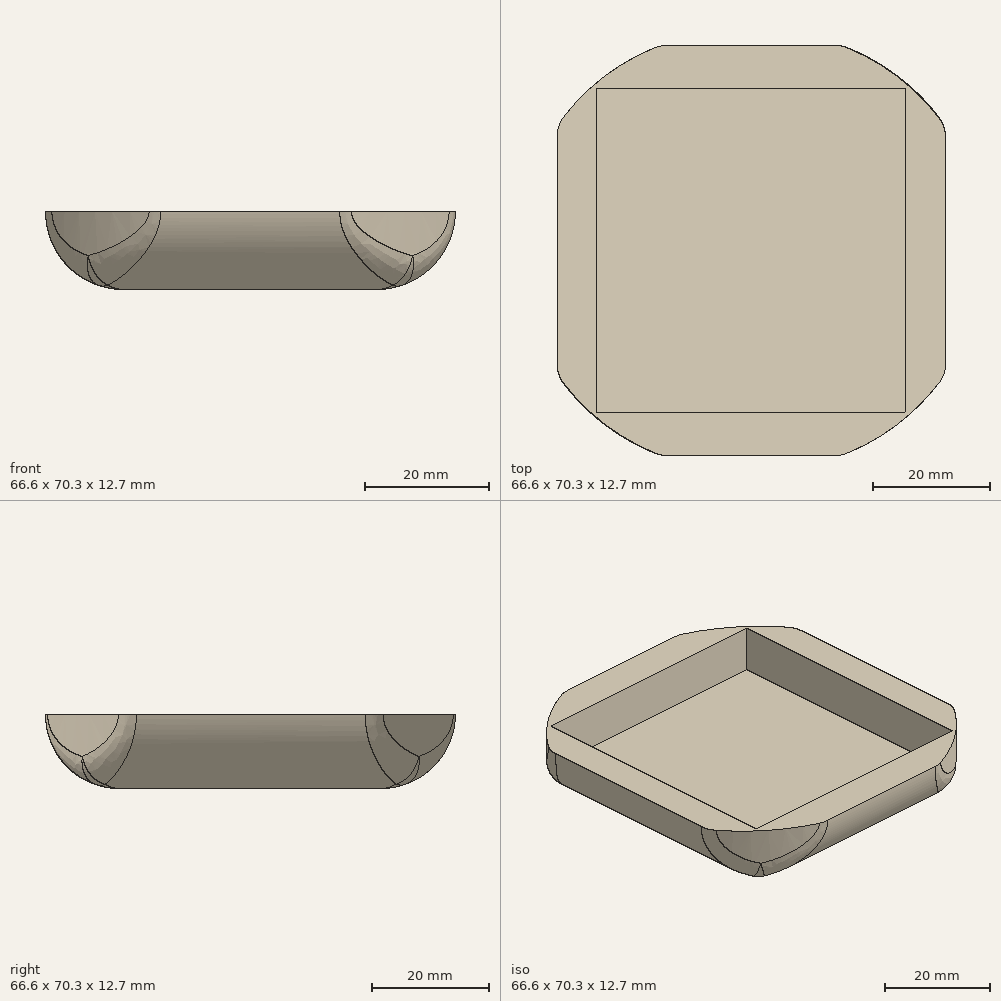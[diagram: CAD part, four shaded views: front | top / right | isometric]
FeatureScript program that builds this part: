
annotation { "Feature Type Name" : "Feature", "Feature Type Description" : "" }
export const myFeature = defineFeature(function(context is Context, id is Id, definition is map)
    precondition{}
    {
        {
            var Q0;
            Q0=qCreatedBy(makeId("Top.planeOp"),FACE);
            var sketch = newSketch(context, id + "F0", { "sketchPlane" : qUnion([Q0])});
            skLineSegment(sketch, "E0.bottom", {"start": v(40, -42.5) * mm, "end": v(-40, -42.5) * mm});
            skLineSegment(sketch, "E0.top", {"start": v(40, 42.5) * mm, "end": v(-40, 42.5) * mm});
            skLineSegment(sketch, "E0.left", {"start": v(40, -42.5) * mm, "end": v(40, 42.5) * mm});
            skLineSegment(sketch, "E0.right", {"start": v(-40, -42.5) * mm, "end": v(-40, 42.5) * mm});
            skPoint(sketch, "E0.middle", {"position": v(0, 0) * mm});
            skSolve(sketch);
        }
        {
            var Q0;
            Q0=makeQuery(id+"F0.imprint","IMPRINT",FACE,{"disambiguationData":[TD([[makeQuery(id+"F0.imprint","IMPRINT",EDGE,{"derivedFrom":sQuery(id+"F0.wireOp",EDGE,"E0.bottom")}),-1.0]])]});
            extrude(context, id + "F1", {"entities" : qUnion([Q0]), "depth" : 25.4 * mm, "offsetDistance" : 25.4 * mm});
        }
        {
            var Q0;
            Q0=qCreatedBy(makeId("Front.planeOp"),FACE);
            var sketch = newSketch(context, id + "F2", { "sketchPlane" : qUnion([Q0])});
            skLineSegment(sketch, "E1.bottom", {"start": v(26.5, 3.57) * mm, "end": v(-26.5, 3.56) * mm});
            skLineSegment(sketch, "E1.top", {"start": v(26.5, 20.57) * mm, "end": v(-26.5, 20.56) * mm});
            skLineSegment(sketch, "E1.left", {"start": v(26.5, 3.57) * mm, "end": v(26.5, 20.57) * mm});
            skLineSegment(sketch, "E1.right", {"start": v(-26.5, 3.56) * mm, "end": v(-26.5, 20.57) * mm});
            skPoint(sketch, "E1.middle", {"position": v(0, 12.07) * mm});
            skSolve(sketch);
        }
        {
            var Q0;
            Q0=qSketchRegion(id+"F2",true);
            extrude(context, id + "F3", {"entities" : qUnion([Q0]), "operationType" : NewBodyOperationType.REMOVE, "oppositeDirection" : true, "depth" : 55.55 * mm, "offsetDistance" : 25.4 * mm, "symmetric" : true});
        }
        {
            var Q0;
            Q0=makeQuery(id+"F1.opExtrude","CAP_FACE",FACE,{"disambiguationData":[OSD([sQuery(id+"F0.wireOp",EDGE,"E0.bottom"),sQuery(id+"F0.wireOp",EDGE,"E0.top"),sQuery(id+"F0.wireOp",EDGE,"E0.left"),sQuery(id+"F0.wireOp",EDGE,"E0.right")])],"isStart":false});
            var sketch = newSketch(context, id + "F4", { "sketchPlane" : qUnion([Q0])});
            skLineSegment(sketch, "E2.bottom", {"start": v(40, -42.5) * mm, "end": v(-40, -42.5) * mm});
            skLineSegment(sketch, "E2.top", {"start": v(40, 42.5) * mm, "end": v(-40, 42.5) * mm});
            skLineSegment(sketch, "E2.left", {"start": v(40, -42.5) * mm, "end": v(40, 42.5) * mm});
            skLineSegment(sketch, "E2.right", {"start": v(-40, -42.5) * mm, "end": v(-40, 42.5) * mm});
            skPoint(sketch, "E2.middle", {"position": v(0, 0) * mm});
            skSolve(sketch);
        }
        {
            var Q0;
            Q0=qSketchRegion(id+"F4",true);
            extrude(context, id + "F5", {"entities" : qUnion([Q0]), "operationType" : NewBodyOperationType.REMOVE, "oppositeDirection" : true, "depth" : 12.7 * mm, "offsetDistance" : 25.4 * mm});
        }
        {
            var Q0;
            Q0=makeQuery(id+"F1.opExtrude","SWEPT_EDGE",EDGE,{"disambiguationData":[OSD([sQuery(id+"F0.wireOp",EDGE,"E0.bottom"),sQuery(id+"F0.wireOp",EDGE,"E0.right")])]});
            fillet(context, id + "F6", {"entities" : qUnion([Q0]), "radius" : 7.62 * mm, "tangentPropagation" : true, "allowEdgeOverflow" : false});
        }
        {
            var Q0;
            Q0=makeQuery(id+"F1.opExtrude","SWEPT_EDGE",EDGE,{"disambiguationData":[OSD([sQuery(id+"F0.wireOp",EDGE,"E0.top"),sQuery(id+"F0.wireOp",EDGE,"E0.right")])]});
            fillet(context, id + "F7", {"entities" : qUnion([Q0]), "radius" : 7.62 * mm, "tangentPropagation" : true, "allowEdgeOverflow" : false});
        }
        {
            var Q0;
            Q0=makeQuery(id+"F1.opExtrude","SWEPT_EDGE",EDGE,{"disambiguationData":[OSD([sQuery(id+"F0.wireOp",EDGE,"E0.top"),sQuery(id+"F0.wireOp",EDGE,"E0.left")])]});
            fillet(context, id + "F8", {"entities" : qUnion([Q0]), "radius" : 7.62 * mm, "tangentPropagation" : true, "allowEdgeOverflow" : false});
        }
        {
            var Q0;
            Q0=makeQuery(id+"F1.opExtrude","SWEPT_EDGE",EDGE,{"disambiguationData":[OSD([sQuery(id+"F0.wireOp",EDGE,"E0.bottom"),sQuery(id+"F0.wireOp",EDGE,"E0.left")])]});
            fillet(context, id + "F9", {"entities" : qUnion([Q0]), "radius" : 7.62 * mm, "tangentPropagation" : true, "allowEdgeOverflow" : false});
        }
        {
            var Q0;
            Q0=makeQuery(id+"F3.boolean.opBoolean","COPY",FACE,{"derivedFrom":makeQuery(id+"F3.opExtrude","SWEPT_FACE",FACE,{"disambiguationData":[OSD([sQuery(id+"F2.wireOp",EDGE,"E1.bottom")])]})});
            var sketch = newSketch(context, id + "F10", { "sketchPlane" : qUnion([Q0])});
            skLineSegment(sketch, "E3", {"start": v(26.5, -42.5) * mm, "end": v(22.69, -35.14) * mm});
            skLineSegment(sketch, "E4", {"start": v(-22.69, -35.14) * mm, "end": v(-26.5, -42.5) * mm});
            skLineSegment(sketch, "E5", {"start": v(40, -27.77) * mm, "end": v(33.33, -24) * mm});
            skLineSegment(sketch, "E6", {"start": v(33.25, 23.96) * mm, "end": v(33.33, -24) * mm});
            skLineSegment(sketch, "E7", {"start": v(40, 27.77) * mm, "end": v(33.25, 23.96) * mm});
            skLineSegment(sketch, "E8", {"start": v(-22.69, 35.14) * mm, "end": v(22.69, 35.14) * mm});
            skLineSegment(sketch, "E9", {"start": v(26.5, 42.5) * mm, "end": v(22.69, 35.14) * mm});
            skLineSegment(sketch, "E10", {"start": v(-26.5, 42.5) * mm, "end": v(-22.69, 35.14) * mm});
            skLineSegment(sketch, "E11", {"start": v(-33.25, 23.96) * mm, "end": v(-33.25, -23.96) * mm});
            skLineSegment(sketch, "E12", {"start": v(-40, 27.77) * mm, "end": v(-33.25, 23.96) * mm});
            skLineSegment(sketch, "E13", {"start": v(-40, -27.77) * mm, "end": v(-33.25, -23.96) * mm});
            skLineSegment(sketch, "E14", {"start": v(40, -27.77) * mm, "end": v(40, 27.77) * mm});
            skLineSegment(sketch, "E15", {"start": v(26.5, 42.5) * mm, "end": v(-26.5, 42.5) * mm});
            skLineSegment(sketch, "E16", {"start": v(-40, 27.77) * mm, "end": v(-40, -27.77) * mm});
            skLineSegment(sketch, "E17", {"start": v(-26.5, -42.5) * mm, "end": v(26.5, -42.5) * mm});
            skLineSegment(sketch, "E18", {"start": v(22.69, -35.14) * mm, "end": v(-22.69, -35.14) * mm});
            skLineSegment(sketch, "E19", {"start": v(40, 27.77) * mm, "end": v(40, -27.77) * mm});
            skSolve(sketch);
        }
        {
            var Q0;
            Q0=qSketchRegion(id+"F10",true);
            extrude(context, id + "F11", {"entities" : qUnion([Q0]), "operationType" : NewBodyOperationType.REMOVE, "depth" : 25.4 * mm, "offsetDistance" : 25.4 * mm, "symmetric" : true});
        }
        {
            var Q0;
            Q0=makeQuery(id+"F1.opExtrude","CAP_FACE",FACE,{"disambiguationData":[OSD([sQuery(id+"F0.wireOp",EDGE,"E0.bottom"),sQuery(id+"F0.wireOp",EDGE,"E0.top"),sQuery(id+"F0.wireOp",EDGE,"E0.left"),sQuery(id+"F0.wireOp",EDGE,"E0.right")])],"isStart":true});
            var sketch = newSketch(context, id + "F12", { "sketchPlane" : qUnion([Q0])});
            skPoint(sketch, "E20.middle", {"position": v(0, 0) * mm});
            skPoint(sketch, "E21.endSnap0", {"position": v(0, 30.06) * mm});
            skLineSegment(sketch, "E22", {"start": v(-15.46, 35.14) * mm, "end": v(0, 35.14) * mm});
            skLineSegment(sketch, "E23", {"start": v(-15.46, 35.14) * mm, "end": v(15.46, 35.14) * mm});
            skLineSegment(sketch, "E24", {"start": v(-15.46, -35.14) * mm, "end": v(15.46, -35.14) * mm});
            skCircle(sketch, "E25", {"center": v(0, 0) * mm, "radius": 62.24 * mm});
            skArc(sketch, "E26", {"start": v(-15.46, 35.14) * mm, "mid": v(-39.89, 0) * mm, "end": v(-15.46, -35.14) * mm});
            skArc(sketch, "E27", {"start": v(15.46, 35.14) * mm, "mid": v(39.89, 0) * mm, "end": v(15.46, -35.14) * mm});
            skSolve(sketch);
        }
        {
            var Q0;
            {var subQ1=sQuery(id+"F0.wireOp",EDGE,"E0.right");var subQ2=sQuery(id+"F0.wireOp",EDGE,"E0.left");var subQ3=sQuery(id+"F0.wireOp",EDGE,"E0.top");var subQ4=sQuery(id+"F0.wireOp",EDGE,"E0.bottom");var subQ5=makeQuery(id+"F1.opExtrude","CAP_FACE",FACE,{"disambiguationData":[OSD([subQ4,subQ3,subQ2,subQ1])],"isStart":true});var subQ6=subQ5;var subQ7=subQ6;var subQ8=subQ7;var subQ9=subQ8;var subQ13=makeQuery(id+"F11.opExtrude","SWEPT_FACE",FACE,{"disambiguationData":[OSD([sQuery(id+"F10.wireOp",EDGE,"E4")])]});var subQ14=makeQuery(id+"F11.boolean.opBoolean","INTERSECT",EDGE,{"derivedFrom":[subQ9,subQ13]});var subQ15=makeQuery(id+"F12.imprint","IMPRINT",EDGE,{"derivedFrom":subQ14});var subQ21=sQuery(id+"F12.wireOp",EDGE,"E22");var subQ35=makeQuery(id+"F11.opExtrude","SWEPT_FACE",FACE,{"disambiguationData":[OSD([sQuery(id+"F10.wireOp",EDGE,"E10")])]});var subQ36=makeQuery(id+"F11.boolean.opBoolean","INTERSECT",EDGE,{"derivedFrom":[subQ9,subQ35]});var subQ41=makeQuery(id+"F12.imprint","IMPRINT",EDGE,{"derivedFrom":subQ36});var subQ52=makeQuery(id+"F11.opExtrude","SWEPT_FACE",FACE,{"disambiguationData":[OSD([sQuery(id+"F10.wireOp",EDGE,"E7")])]});var subQ53=makeQuery(id+"F11.boolean.opBoolean","INTERSECT",EDGE,{"derivedFrom":[subQ9,subQ52]});var subQ54=makeQuery(id+"F12.imprint","IMPRINT",EDGE,{"derivedFrom":subQ53});var subQ70=makeQuery(id+"F11.opExtrude","SWEPT_FACE",FACE,{"disambiguationData":[OSD([sQuery(id+"F10.wireOp",EDGE,"E3")])]});var subQ71=makeQuery(id+"F11.boolean.opBoolean","INTERSECT",EDGE,{"derivedFrom":[subQ9,subQ70]});var subQ72=makeQuery(id+"F12.imprint","IMPRINT",EDGE,{"derivedFrom":subQ71});Q0=qUnion([makeQuery(id+"F12.imprint","IMPRINT",FACE,{"disambiguationData":[TD([[subQ72,-1.0]])]}),makeQuery(id+"F12.imprint","IMPRINT",FACE,{"disambiguationData":[TD([[makeQuery(id+"F12.imprint","IMPRINT",EDGE,{"derivedFrom":subQ21}),1.0]])]}),makeQuery(id+"F12.imprint","IMPRINT",FACE,{"disambiguationData":[TD([[subQ54,-1.0]])]}),makeQuery(id+"F12.imprint","IMPRINT",FACE,{"disambiguationData":[TD([[subQ41,-1.0]])]}),makeQuery(id+"F12.imprint","IMPRINT",FACE,{"disambiguationData":[TD([[subQ15,-1.0]])]})]);}
            extrude(context, id + "F13", {"entities" : qUnion([Q0]), "operationType" : NewBodyOperationType.REMOVE, "oppositeDirection" : true, "depth" : 25.4 * mm, "offsetDistance" : 25.4 * mm});
        }
        {
            var Q0;
            Q0=makeQuery(id+"F11.boolean.opBoolean","INTERSECT",EDGE,{"derivedFrom":[makeQuery(id+"F1.opExtrude","CAP_FACE",FACE,{"disambiguationData":[OSD([sQuery(id+"F0.wireOp",EDGE,"E0.bottom"),sQuery(id+"F0.wireOp",EDGE,"E0.top"),sQuery(id+"F0.wireOp",EDGE,"E0.left"),sQuery(id+"F0.wireOp",EDGE,"E0.right")])],"isStart":true}),makeQuery(id+"F11.opExtrude","SWEPT_FACE",FACE,{"disambiguationData":[OSD([sQuery(id+"F10.wireOp",EDGE,"E18")])]})]});
            fillet(context, id + "F14", {"entities" : qUnion([Q0]), "radius" : 12.7 * mm, "tangentPropagation" : true, "allowEdgeOverflow" : false});
        }
        {
            var Q0;
            Q0=makeQuery(id+"F11.boolean.opBoolean","INTERSECT",EDGE,{"derivedFrom":[makeQuery(id+"F1.opExtrude","CAP_FACE",FACE,{"disambiguationData":[OSD([sQuery(id+"F0.wireOp",EDGE,"E0.bottom"),sQuery(id+"F0.wireOp",EDGE,"E0.top"),sQuery(id+"F0.wireOp",EDGE,"E0.left"),sQuery(id+"F0.wireOp",EDGE,"E0.right")])],"isStart":true}),makeQuery(id+"F11.opExtrude","SWEPT_FACE",FACE,{"disambiguationData":[OSD([sQuery(id+"F10.wireOp",EDGE,"E6")])]})]});
            fillet(context, id + "F15", {"entities" : qUnion([Q0]), "radius" : 12.7 * mm, "tangentPropagation" : true, "allowEdgeOverflow" : false});
        }
        {
            var Q0;
            Q0=makeQuery(id+"F11.boolean.opBoolean","INTERSECT",EDGE,{"derivedFrom":[makeQuery(id+"F1.opExtrude","CAP_FACE",FACE,{"disambiguationData":[OSD([sQuery(id+"F0.wireOp",EDGE,"E0.bottom"),sQuery(id+"F0.wireOp",EDGE,"E0.top"),sQuery(id+"F0.wireOp",EDGE,"E0.left"),sQuery(id+"F0.wireOp",EDGE,"E0.right")])],"isStart":true}),makeQuery(id+"F11.opExtrude","SWEPT_FACE",FACE,{"disambiguationData":[OSD([sQuery(id+"F10.wireOp",EDGE,"E8")])]})]});
            fillet(context, id + "F16", {"entities" : qUnion([Q0]), "radius" : 12.7 * mm, "tangentPropagation" : true, "allowEdgeOverflow" : false});
        }
        {
            var Q0;
            Q0=makeQuery(id+"F11.boolean.opBoolean","INTERSECT",EDGE,{"derivedFrom":[makeQuery(id+"F1.opExtrude","CAP_FACE",FACE,{"disambiguationData":[OSD([sQuery(id+"F0.wireOp",EDGE,"E0.bottom"),sQuery(id+"F0.wireOp",EDGE,"E0.top"),sQuery(id+"F0.wireOp",EDGE,"E0.left"),sQuery(id+"F0.wireOp",EDGE,"E0.right")])],"isStart":true}),makeQuery(id+"F11.opExtrude","SWEPT_FACE",FACE,{"disambiguationData":[OSD([sQuery(id+"F10.wireOp",EDGE,"E11")])]})]});
            fillet(context, id + "F17", {"entities" : qUnion([Q0]), "radius" : 12.7 * mm, "tangentPropagation" : true, "allowEdgeOverflow" : false});
        }
        {
            var Q0;
            {var subQ0=makeQuery(id+"F1.opExtrude","CAP_FACE",FACE,{"disambiguationData":[OSD([sQuery(id+"F0.wireOp",EDGE,"E0.bottom"),sQuery(id+"F0.wireOp",EDGE,"E0.top"),sQuery(id+"F0.wireOp",EDGE,"E0.left"),sQuery(id+"F0.wireOp",EDGE,"E0.right")])],"isStart":true});var subQ1=makeQuery(id+"F11.opExtrude","SWEPT_FACE",FACE,{"disambiguationData":[OSD([sQuery(id+"F10.wireOp",EDGE,"E6")])]});Q0=makeQuery(id+"F15.opFillet","BLEND_EDGE",EDGE,{"blendedFrom":[makeQuery(id+"F11.boolean.opBoolean","INTERSECT",EDGE,{"derivedFrom":[subQ0,subQ1]}),makeQuery(id+"F13.boolean.opBoolean","COPY",FACE,{"disambiguationData":[TD([makeQuery(id+"F11.boolean.opBoolean","COPY",FACE,{"derivedFrom":makeQuery(id+"F11.opExtrude","SWEPT_FACE",FACE,{"disambiguationData":[OSD([sQuery(id+"F10.wireOp",EDGE,"E18")])]})})])],"derivedFrom":makeQuery(id+"F13.opExtrude","SWEPT_FACE",FACE,{"disambiguationData":[OSD([sQuery(id+"F12.wireOp",EDGE,"E27")])]})})],"blendedInto":[makeQuery(id+"F13.boolean.opBoolean","COPY",FACE,{"disambiguationData":[TD([makeQuery(id+"F11.boolean.opBoolean","COPY",FACE,{"derivedFrom":makeQuery(id+"F11.opExtrude","SWEPT_FACE",FACE,{"disambiguationData":[OSD([sQuery(id+"F10.wireOp",EDGE,"E18")])]})})])],"derivedFrom":makeQuery(id+"F13.opExtrude","SWEPT_FACE",FACE,{"disambiguationData":[OSD([sQuery(id+"F12.wireOp",EDGE,"E27")])]})})]});}
            fillet(context, id + "F18", {"entities" : qUnion([Q0]), "radius" : 5.08 * mm, "tangentPropagation" : true, "allowEdgeOverflow" : false});
        }
        {
            var Q0;
            {var subQ0=sQuery(id+"F10.wireOp",EDGE,"E18");var subQ1=sQuery(id+"F0.wireOp",EDGE,"E0.right");var subQ2=sQuery(id+"F0.wireOp",EDGE,"E0.left");var subQ3=sQuery(id+"F0.wireOp",EDGE,"E0.top");var subQ4=sQuery(id+"F0.wireOp",EDGE,"E0.bottom");var subQ5=makeQuery(id+"F1.opExtrude","CAP_FACE",FACE,{"disambiguationData":[OSD([subQ4,subQ3,subQ2,subQ1])],"isStart":true});var subQ6=makeQuery(id+"F11.opExtrude","SWEPT_FACE",FACE,{"disambiguationData":[OSD([sQuery(id+"F10.wireOp",EDGE,"E6")])]});Q0=makeQuery(id+"F18.opFillet","BLEND_EDGE",EDGE,{"blendedFrom":[makeQuery(id+"F15.opFillet","BLEND_EDGE",EDGE,{"blendedFrom":[makeQuery(id+"F11.boolean.opBoolean","INTERSECT",EDGE,{"derivedFrom":[subQ5,subQ6]}),makeQuery(id+"F13.boolean.opBoolean","COPY",FACE,{"disambiguationData":[TD([makeQuery(id+"F11.boolean.opBoolean","COPY",FACE,{"derivedFrom":makeQuery(id+"F11.opExtrude","SWEPT_FACE",FACE,{"disambiguationData":[OSD([subQ0])]})})])],"derivedFrom":makeQuery(id+"F13.opExtrude","SWEPT_FACE",FACE,{"disambiguationData":[OSD([sQuery(id+"F12.wireOp",EDGE,"E27")])]})})],"blendedInto":[makeQuery(id+"F13.boolean.opBoolean","COPY",FACE,{"disambiguationData":[TD([makeQuery(id+"F11.boolean.opBoolean","COPY",FACE,{"derivedFrom":makeQuery(id+"F11.opExtrude","SWEPT_FACE",FACE,{"disambiguationData":[OSD([subQ0])]})})])],"derivedFrom":makeQuery(id+"F13.opExtrude","SWEPT_FACE",FACE,{"disambiguationData":[OSD([sQuery(id+"F12.wireOp",EDGE,"E27")])]})})]}),makeQuery(id+"F14.opFillet","BLEND_FACE",FACE,{"disambiguationData":[OSD([subQ4,subQ3,subQ2,subQ1,subQ0])]})],"blendedInto":[makeQuery(id+"F14.opFillet","BLEND_FACE",FACE,{"disambiguationData":[OSD([subQ4,subQ3,subQ2,subQ1,subQ0])]})]});}
            fillet(context, id + "F19", {"entities" : qUnion([Q0]), "radius" : 5.08 * mm, "tangentPropagation" : true, "allowEdgeOverflow" : false});
        }
        {
            var Q0;
            {var subQ0=makeQuery(id+"F1.opExtrude","CAP_FACE",FACE,{"disambiguationData":[OSD([sQuery(id+"F0.wireOp",EDGE,"E0.bottom"),sQuery(id+"F0.wireOp",EDGE,"E0.top"),sQuery(id+"F0.wireOp",EDGE,"E0.left"),sQuery(id+"F0.wireOp",EDGE,"E0.right")])],"isStart":true});var subQ1=makeQuery(id+"F11.opExtrude","SWEPT_FACE",FACE,{"disambiguationData":[OSD([sQuery(id+"F10.wireOp",EDGE,"E6")])]});Q0=makeQuery(id+"F15.opFillet","BLEND_EDGE",EDGE,{"blendedFrom":[makeQuery(id+"F11.boolean.opBoolean","INTERSECT",EDGE,{"derivedFrom":[subQ0,subQ1]}),makeQuery(id+"F13.boolean.opBoolean","COPY",FACE,{"disambiguationData":[TD([makeQuery(id+"F11.boolean.opBoolean","COPY",FACE,{"derivedFrom":makeQuery(id+"F11.opExtrude","SWEPT_FACE",FACE,{"disambiguationData":[OSD([sQuery(id+"F10.wireOp",EDGE,"E8")])]})})])],"derivedFrom":makeQuery(id+"F13.opExtrude","SWEPT_FACE",FACE,{"disambiguationData":[OSD([sQuery(id+"F12.wireOp",EDGE,"E27")])]})})],"blendedInto":[makeQuery(id+"F13.boolean.opBoolean","COPY",FACE,{"disambiguationData":[TD([makeQuery(id+"F11.boolean.opBoolean","COPY",FACE,{"derivedFrom":makeQuery(id+"F11.opExtrude","SWEPT_FACE",FACE,{"disambiguationData":[OSD([sQuery(id+"F10.wireOp",EDGE,"E8")])]})})])],"derivedFrom":makeQuery(id+"F13.opExtrude","SWEPT_FACE",FACE,{"disambiguationData":[OSD([sQuery(id+"F12.wireOp",EDGE,"E27")])]})})]});}
            fillet(context, id + "F20", {"entities" : qUnion([Q0]), "radius" : 5.08 * mm, "tangentPropagation" : true, "allowEdgeOverflow" : false});
        }
        {
            var Q0;
            {var subQ0=makeQuery(id+"F1.opExtrude","CAP_FACE",FACE,{"disambiguationData":[OSD([sQuery(id+"F0.wireOp",EDGE,"E0.bottom"),sQuery(id+"F0.wireOp",EDGE,"E0.top"),sQuery(id+"F0.wireOp",EDGE,"E0.left"),sQuery(id+"F0.wireOp",EDGE,"E0.right")])],"isStart":true});var subQ1=makeQuery(id+"F11.opExtrude","SWEPT_FACE",FACE,{"disambiguationData":[OSD([sQuery(id+"F10.wireOp",EDGE,"E8")])]});Q0=makeQuery(id+"F16.opFillet","BLEND_EDGE",EDGE,{"blendedFrom":[makeQuery(id+"F11.boolean.opBoolean","INTERSECT",EDGE,{"derivedFrom":[subQ0,subQ1]}),makeQuery(id+"F13.boolean.opBoolean","COPY",FACE,{"disambiguationData":[TD([makeQuery(id+"F11.boolean.opBoolean","COPY",FACE,{"derivedFrom":subQ1})])],"derivedFrom":makeQuery(id+"F13.opExtrude","SWEPT_FACE",FACE,{"disambiguationData":[OSD([sQuery(id+"F12.wireOp",EDGE,"E27")])]})})],"blendedInto":[makeQuery(id+"F13.boolean.opBoolean","COPY",FACE,{"disambiguationData":[TD([makeQuery(id+"F11.boolean.opBoolean","COPY",FACE,{"derivedFrom":subQ1})])],"derivedFrom":makeQuery(id+"F13.opExtrude","SWEPT_FACE",FACE,{"disambiguationData":[OSD([sQuery(id+"F12.wireOp",EDGE,"E27")])]})})]});}
            fillet(context, id + "F21", {"entities" : qUnion([Q0]), "radius" : 5.08 * mm, "tangentPropagation" : true, "allowEdgeOverflow" : false});
        }
        {
            var Q0;
            {var subQ0=makeQuery(id+"F1.opExtrude","CAP_FACE",FACE,{"disambiguationData":[OSD([sQuery(id+"F0.wireOp",EDGE,"E0.bottom"),sQuery(id+"F0.wireOp",EDGE,"E0.top"),sQuery(id+"F0.wireOp",EDGE,"E0.left"),sQuery(id+"F0.wireOp",EDGE,"E0.right")])],"isStart":true});var subQ1=makeQuery(id+"F11.opExtrude","SWEPT_FACE",FACE,{"disambiguationData":[OSD([sQuery(id+"F10.wireOp",EDGE,"E8")])]});Q0=makeQuery(id+"F16.opFillet","BLEND_EDGE",EDGE,{"blendedFrom":[makeQuery(id+"F11.boolean.opBoolean","INTERSECT",EDGE,{"derivedFrom":[subQ0,subQ1]}),makeQuery(id+"F13.boolean.opBoolean","COPY",FACE,{"disambiguationData":[TD([makeQuery(id+"F11.boolean.opBoolean","COPY",FACE,{"derivedFrom":subQ1})])],"derivedFrom":makeQuery(id+"F13.opExtrude","SWEPT_FACE",FACE,{"disambiguationData":[OSD([sQuery(id+"F12.wireOp",EDGE,"E26")])]})})],"blendedInto":[makeQuery(id+"F13.boolean.opBoolean","COPY",FACE,{"disambiguationData":[TD([makeQuery(id+"F11.boolean.opBoolean","COPY",FACE,{"derivedFrom":subQ1})])],"derivedFrom":makeQuery(id+"F13.opExtrude","SWEPT_FACE",FACE,{"disambiguationData":[OSD([sQuery(id+"F12.wireOp",EDGE,"E26")])]})})]});}
            fillet(context, id + "F22", {"entities" : qUnion([Q0]), "radius" : 5.08 * mm, "tangentPropagation" : true, "allowEdgeOverflow" : false});
        }
        {
            var Q0;
            {var subQ0=makeQuery(id+"F1.opExtrude","CAP_FACE",FACE,{"disambiguationData":[OSD([sQuery(id+"F0.wireOp",EDGE,"E0.bottom"),sQuery(id+"F0.wireOp",EDGE,"E0.top"),sQuery(id+"F0.wireOp",EDGE,"E0.left"),sQuery(id+"F0.wireOp",EDGE,"E0.right")])],"isStart":true});var subQ1=makeQuery(id+"F11.opExtrude","SWEPT_FACE",FACE,{"disambiguationData":[OSD([sQuery(id+"F10.wireOp",EDGE,"E11")])]});Q0=makeQuery(id+"F17.opFillet","BLEND_EDGE",EDGE,{"blendedFrom":[makeQuery(id+"F11.boolean.opBoolean","INTERSECT",EDGE,{"derivedFrom":[subQ0,subQ1]}),makeQuery(id+"F13.boolean.opBoolean","COPY",FACE,{"disambiguationData":[TD([makeQuery(id+"F11.boolean.opBoolean","COPY",FACE,{"derivedFrom":makeQuery(id+"F11.opExtrude","SWEPT_FACE",FACE,{"disambiguationData":[OSD([sQuery(id+"F10.wireOp",EDGE,"E8")])]})})])],"derivedFrom":makeQuery(id+"F13.opExtrude","SWEPT_FACE",FACE,{"disambiguationData":[OSD([sQuery(id+"F12.wireOp",EDGE,"E26")])]})})],"blendedInto":[makeQuery(id+"F13.boolean.opBoolean","COPY",FACE,{"disambiguationData":[TD([makeQuery(id+"F11.boolean.opBoolean","COPY",FACE,{"derivedFrom":makeQuery(id+"F11.opExtrude","SWEPT_FACE",FACE,{"disambiguationData":[OSD([sQuery(id+"F10.wireOp",EDGE,"E8")])]})})])],"derivedFrom":makeQuery(id+"F13.opExtrude","SWEPT_FACE",FACE,{"disambiguationData":[OSD([sQuery(id+"F12.wireOp",EDGE,"E26")])]})})]});}
            fillet(context, id + "F23", {"entities" : qUnion([Q0]), "radius" : 5.08 * mm, "tangentPropagation" : true, "allowEdgeOverflow" : false});
        }
        {
            var Q0;
            {var subQ0=makeQuery(id+"F1.opExtrude","CAP_FACE",FACE,{"disambiguationData":[OSD([sQuery(id+"F0.wireOp",EDGE,"E0.bottom"),sQuery(id+"F0.wireOp",EDGE,"E0.top"),sQuery(id+"F0.wireOp",EDGE,"E0.left"),sQuery(id+"F0.wireOp",EDGE,"E0.right")])],"isStart":true});var subQ1=makeQuery(id+"F11.opExtrude","SWEPT_FACE",FACE,{"disambiguationData":[OSD([sQuery(id+"F10.wireOp",EDGE,"E11")])]});Q0=makeQuery(id+"F17.opFillet","BLEND_EDGE",EDGE,{"blendedFrom":[makeQuery(id+"F11.boolean.opBoolean","INTERSECT",EDGE,{"derivedFrom":[subQ0,subQ1]}),makeQuery(id+"F13.boolean.opBoolean","COPY",FACE,{"disambiguationData":[TD([makeQuery(id+"F11.boolean.opBoolean","COPY",FACE,{"derivedFrom":makeQuery(id+"F11.opExtrude","SWEPT_FACE",FACE,{"disambiguationData":[OSD([sQuery(id+"F10.wireOp",EDGE,"E18")])]})})])],"derivedFrom":makeQuery(id+"F13.opExtrude","SWEPT_FACE",FACE,{"disambiguationData":[OSD([sQuery(id+"F12.wireOp",EDGE,"E26")])]})})],"blendedInto":[makeQuery(id+"F13.boolean.opBoolean","COPY",FACE,{"disambiguationData":[TD([makeQuery(id+"F11.boolean.opBoolean","COPY",FACE,{"derivedFrom":makeQuery(id+"F11.opExtrude","SWEPT_FACE",FACE,{"disambiguationData":[OSD([sQuery(id+"F10.wireOp",EDGE,"E18")])]})})])],"derivedFrom":makeQuery(id+"F13.opExtrude","SWEPT_FACE",FACE,{"disambiguationData":[OSD([sQuery(id+"F12.wireOp",EDGE,"E26")])]})})]});}
            fillet(context, id + "F24", {"entities" : qUnion([Q0]), "radius" : 5.08 * mm, "tangentPropagation" : true, "allowEdgeOverflow" : false});
        }
        {
            var Q0;
            {var subQ0=sQuery(id+"F10.wireOp",EDGE,"E18");var subQ1=sQuery(id+"F0.wireOp",EDGE,"E0.right");var subQ2=sQuery(id+"F0.wireOp",EDGE,"E0.left");var subQ3=sQuery(id+"F0.wireOp",EDGE,"E0.top");var subQ4=sQuery(id+"F0.wireOp",EDGE,"E0.bottom");var subQ5=makeQuery(id+"F1.opExtrude","CAP_FACE",FACE,{"disambiguationData":[OSD([subQ4,subQ3,subQ2,subQ1])],"isStart":true});var subQ6=makeQuery(id+"F11.opExtrude","SWEPT_FACE",FACE,{"disambiguationData":[OSD([sQuery(id+"F10.wireOp",EDGE,"E11")])]});Q0=makeQuery(id+"F24.opFillet","BLEND_EDGE",EDGE,{"blendedFrom":[makeQuery(id+"F17.opFillet","BLEND_EDGE",EDGE,{"blendedFrom":[makeQuery(id+"F11.boolean.opBoolean","INTERSECT",EDGE,{"derivedFrom":[subQ5,subQ6]}),makeQuery(id+"F13.boolean.opBoolean","COPY",FACE,{"disambiguationData":[TD([makeQuery(id+"F11.boolean.opBoolean","COPY",FACE,{"derivedFrom":makeQuery(id+"F11.opExtrude","SWEPT_FACE",FACE,{"disambiguationData":[OSD([subQ0])]})})])],"derivedFrom":makeQuery(id+"F13.opExtrude","SWEPT_FACE",FACE,{"disambiguationData":[OSD([sQuery(id+"F12.wireOp",EDGE,"E26")])]})})],"blendedInto":[makeQuery(id+"F13.boolean.opBoolean","COPY",FACE,{"disambiguationData":[TD([makeQuery(id+"F11.boolean.opBoolean","COPY",FACE,{"derivedFrom":makeQuery(id+"F11.opExtrude","SWEPT_FACE",FACE,{"disambiguationData":[OSD([subQ0])]})})])],"derivedFrom":makeQuery(id+"F13.opExtrude","SWEPT_FACE",FACE,{"disambiguationData":[OSD([sQuery(id+"F12.wireOp",EDGE,"E26")])]})})]}),makeQuery(id+"F14.opFillet","BLEND_FACE",FACE,{"disambiguationData":[OSD([subQ4,subQ3,subQ2,subQ1,subQ0])]})],"blendedInto":[makeQuery(id+"F14.opFillet","BLEND_FACE",FACE,{"disambiguationData":[OSD([subQ4,subQ3,subQ2,subQ1,subQ0])]})]});}
            fillet(context, id + "F25", {"entities" : qUnion([Q0]), "radius" : 5.08 * mm, "tangentPropagation" : true, "allowEdgeOverflow" : false});
        }
    });
